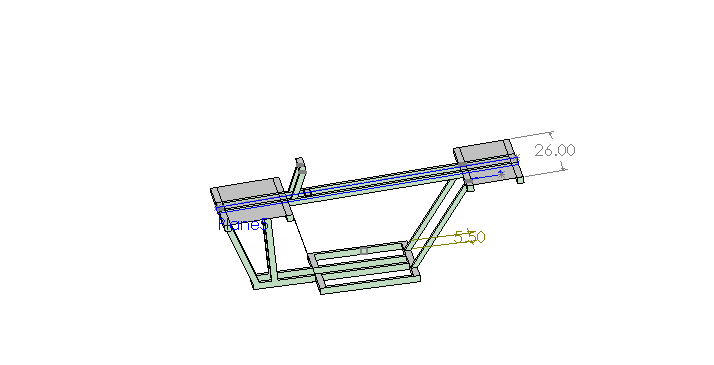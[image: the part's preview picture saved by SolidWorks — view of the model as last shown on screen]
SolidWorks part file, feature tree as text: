
SOLIDWORKS PART (.sldprt)
format: sldprt  version: not decoded by parser v0  size: 593,920 bytes
history: native  units: mm
features: sketch x23, extrude x6, plane x5, sweep x3 + 1 further entry (+10 scaffold rows collapsed)
feature tree (48):
  "Annotations"  RD1=660.4mm RD2=139.7mm
  scaffold x10  (default folders/planes/origin — collapsed)
  sketch  "Sketch1"  dims[D1=152.4mm D2=152.4mm D3=965.2mm D4=254.0mm D5=50.8mm D6=25.4mm]
  extrude  "Extrude1"  Depth=25.4mm
  plane  "Plane1"  Offset=355.6mm
  plane  "Plane3"
  plane  "Plane4"  Offset=355.6mm
  sketch  "Sketch4"  dims[c1.D1=609.6mm c1.D2=228.6mm c1.D3=2.54mm c1.D5=406.4mm c1.D6=457.2mm c1.D7=203.2mm c2.D3=101.6mm c2.D8=25.4mm c2.D9=25.4mm c2.D10=228.6mm c2.D11=203.2mm c2.D7=25.4mm c2.D4=25.4mm]
  extrude  "Extrude3"  Depth=25.4mm
  sketch  "Sketch5"  dims[D1=139.7mm D2=139.7mm]
  sketch  "Sketch6"  dims[c1.D1=25.4mm c1.D2=228.6mm c2.D1=139.7mm c2.D2=139.7mm]
  sketch  "3DSketch2"
  sweep  "Sweep1"
  sketch  "Sketch7"
  sketch  "Sketch8"
  sketch  "3DSketch3"
  sweep  "Sweep2"
  sketch  "Sketch16"  dims[D1=50.8mm D2=25.4mm]
  extrude  "Extrude10"  [1 undecoded]
  sketch  "Sketch9"  dims[D1=50.8mm D2=1.5875mm]
  extrude  "Extrude4"  [1 undecoded]
  plane  "Plane2"  Offset=101.6mm
  sketch  "Sketch10"  dims[c1.D1=25.4mm c1.D2=127.0mm c1.D3=101.6mm c2.D1=25.4mm c2.D2=127.0mm]
  sketch  "Sketch12"  dims[D1=25.4mm D2=177.8mm]
  sketch  "3DSketch5"
  sweep  "Sweep3"
  sketch  "Sketch13"  dims[D1=25.4mm]
  extrude  "Extrude6"  [1 undecoded]
  sketch  "Sketch17"  dims[D1=25.4mm]
  sketch  "Sketch18"  dims[D1=25.4mm D2=254.0mm D3=177.8mm]
  extrude  "Extrude13"  Depth=254mm
  sketch  "Sketch19"
  plane  "Plane5"  Offset=50.8mm
  sketch  "Sketch29"
  sketch  "Sketch30"
  sketch  "Sketch31"
  sketch  "Sketch33"
  sketch  "Sketch34"
  sketch  "Sketch35"
decode coverage: 14 of 32 modeling features carry decoded parameters; 1 rows unclassified (native names shown)
note: 3 parameter values undecoded
summary: no parameter record found for 3 features
note: suppression state not decoded; provenance and decode notes live in map.json
